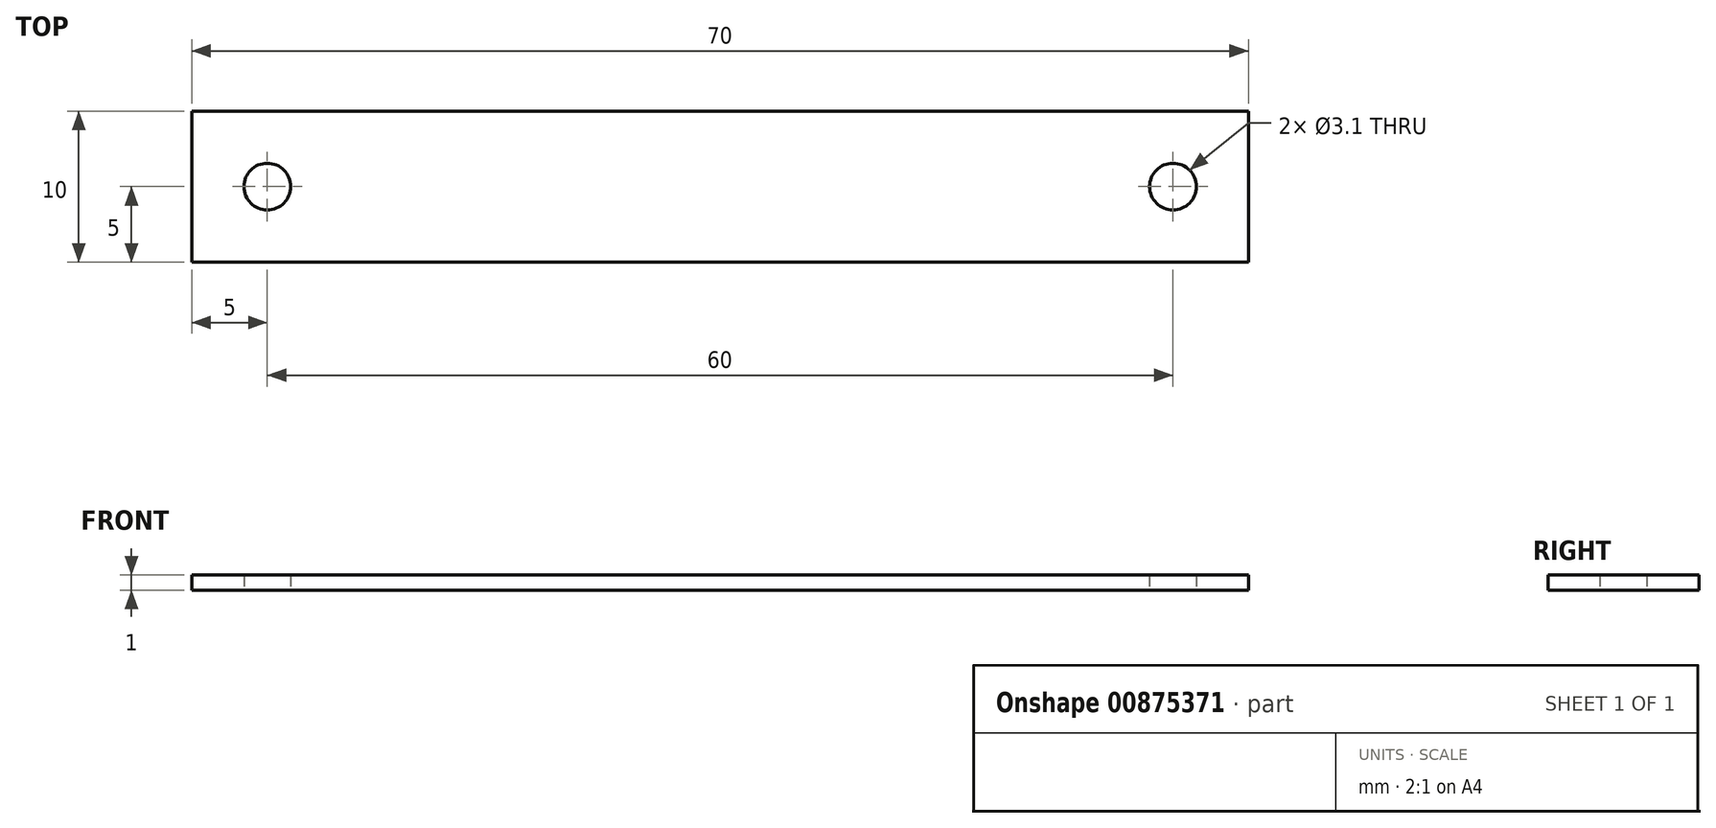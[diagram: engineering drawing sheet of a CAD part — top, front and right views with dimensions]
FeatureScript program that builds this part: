
annotation { "Feature Type Name" : "Feature", "Feature Type Description" : "" }
export const myFeature = defineFeature(function(context is Context, id is Id, definition is map)
    precondition{}
    {
        {
            var Q0;
            Q0=qCreatedBy(makeId("Top.planeOp"),FACE);
            var sketch = newSketch(context, id + "F0", { "sketchPlane" : qUnion([Q0])});
            skLineSegment(sketch, "E0.bottom", {"start": v(35, 5) * mm, "end": v(-35, 5) * mm});
            skLineSegment(sketch, "E0.top", {"start": v(35, -5) * mm, "end": v(-35, -5) * mm});
            skLineSegment(sketch, "E0.left", {"start": v(35, 5) * mm, "end": v(35, -5) * mm});
            skLineSegment(sketch, "E0.right", {"start": v(-35, 5) * mm, "end": v(-35, -5) * mm});
            skPoint(sketch, "E0.middle", {"position": v(0, 0) * mm});
            skCircle(sketch, "E1", {"center": v(-30, 0) * mm, "radius": 1.55 * mm});
            skCircle(sketch, "E2", {"center": v(30, 0) * mm, "radius": 1.55 * mm});
            skSolve(sketch);
        }
        {
            var Q0;
            Q0=makeQuery(id+"F0.imprint","IMPRINT",FACE,{"disambiguationData":[TD([[makeQuery(id+"F0.imprint","IMPRINT",EDGE,{"derivedFrom":sQuery(id+"F0.wireOp",EDGE,"E0.bottom")}),1.0]])]});
            extrude(context, id + "F1", {"entities" : qUnion([Q0]), "depth" : 1 * mm, "offsetDistance" : 25 * mm});
        }
    });
